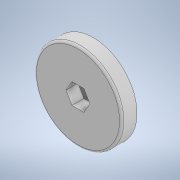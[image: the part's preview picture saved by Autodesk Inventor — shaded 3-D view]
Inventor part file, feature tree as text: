
AUTODESK INVENTOR PART (.ipt)
format: ipt  version: 2020 (Build 240168000, 168)  size: 158,208 bytes
history: native  units: mm
features: sketch x3, extrude x3, other x2, revolve x1, fillet x1
ambient origin geometry x8: Origin, YZ Plane, XZ Plane, XY Plane, X Axis, Y Axis, Z Axis, Center Point
bodies: Body1 (feature_tree)
feature tree (10):
  other  "Твердое тело1"
  sketch  "Эскиз1"
  revolve  "Вращение1"
  other  "РабПлоскость2"
  extrude  "Выдавливание4"  Depth=20.0mm
  sketch  "Эскиз4"
  extrude  "Выдавливание5"  Depth=3.5mm
  extrude  "Выдавливание6"  Depth=5.0mm
  fillet  "Сопряжение1"  Radius=2.0mm
  sketch  "Эскиз3"
